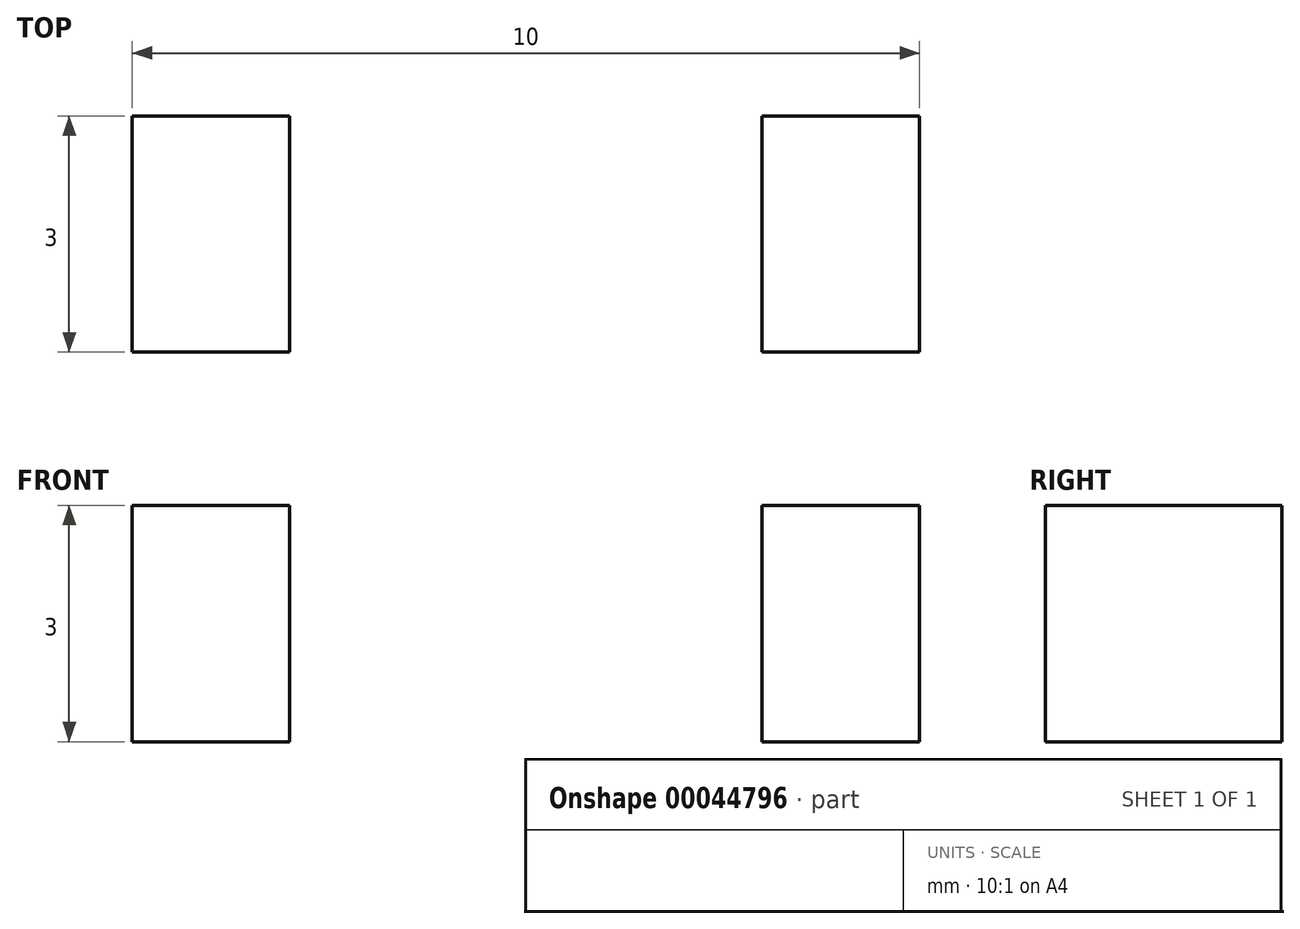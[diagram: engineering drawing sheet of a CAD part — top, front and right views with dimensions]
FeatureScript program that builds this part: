
annotation { "Feature Type Name" : "Feature", "Feature Type Description" : "" }
export const myFeature = defineFeature(function(context is Context, id is Id, definition is map)
    precondition{}
    {
        {
            var Q0;
            Q0=qCreatedBy(makeId("Front.planeOp"),FACE);
            var sketch = newSketch(context, id + "F0", { "sketchPlane" : qUnion([Q0])});
            skLineSegment(sketch, "E0.rect.bottom", {"start": v(5, 42) * mm, "end": v(-5, 42) * mm});
            skLineSegment(sketch, "E0.rect.top", {"start": v(5, -42) * mm, "end": v(-5, -42) * mm});
            skLineSegment(sketch, "E0.rect.left", {"start": v(5, 42) * mm, "end": v(5, -42) * mm});
            skLineSegment(sketch, "E0.rect.right", {"start": v(-5, 42) * mm, "end": v(-5, -42) * mm});
            skPoint(sketch, "E0.rect.middle", {"position": v(0, 0) * mm});
            skLineSegment(sketch, "E1", {"start": v(0, 42) * mm, "end": v(0, -42) * mm, "construction": true});
            skCircle(sketch, "E2", {"center": v(0, 27) * mm, "radius": 1.5 * mm});
            skCircle(sketch, "E3", {"center": v(0, -33) * mm, "radius": 1.5 * mm});
            skLineSegment(sketch, "E4.bottom", {"start": v(-5, 22) * mm, "end": v(-3, 22) * mm});
            skLineSegment(sketch, "E4.top", {"start": v(-5, 25) * mm, "end": v(-3, 25) * mm});
            skLineSegment(sketch, "E4.left", {"start": v(-5, 22) * mm, "end": v(-5, 25) * mm});
            skLineSegment(sketch, "E4.right", {"start": v(-3, 22) * mm, "end": v(-3, 25) * mm});
            skLineSegment(sketch, "E5.bottom", {"start": v(5, 22) * mm, "end": v(3, 22) * mm});
            skLineSegment(sketch, "E5.top", {"start": v(5, 25) * mm, "end": v(3, 25) * mm});
            skLineSegment(sketch, "E5.left", {"start": v(5, 22) * mm, "end": v(5, 25) * mm});
            skLineSegment(sketch, "E5.right", {"start": v(3, 22) * mm, "end": v(3, 25) * mm});
            skLineSegment(sketch, "E6.bottom", {"start": v(-5, -31) * mm, "end": v(-3, -31) * mm});
            skLineSegment(sketch, "E6.top", {"start": v(-5, -28) * mm, "end": v(-3, -28) * mm});
            skLineSegment(sketch, "E6.left", {"start": v(-5, -31) * mm, "end": v(-5, -28) * mm});
            skLineSegment(sketch, "E6.right", {"start": v(-3, -31) * mm, "end": v(-3, -28) * mm});
            skLineSegment(sketch, "E7.bottom", {"start": v(5, -31) * mm, "end": v(3, -31) * mm});
            skLineSegment(sketch, "E7.top", {"start": v(5, -28) * mm, "end": v(3, -28) * mm});
            skLineSegment(sketch, "E7.left", {"start": v(5, -31) * mm, "end": v(5, -28) * mm});
            skLineSegment(sketch, "E7.right", {"start": v(3, -31) * mm, "end": v(3, -28) * mm});
            skLineSegment(sketch, "E8.bottom", {"start": v(-5, 42) * mm, "end": v(-3, 42) * mm});
            skLineSegment(sketch, "E8.top", {"start": v(-5, 39) * mm, "end": v(-3, 39) * mm});
            skLineSegment(sketch, "E8.left", {"start": v(-5, 42) * mm, "end": v(-5, 39) * mm});
            skLineSegment(sketch, "E8.right", {"start": v(-3, 42) * mm, "end": v(-3, 39) * mm});
            skLineSegment(sketch, "E9.bottom", {"start": v(5, 42) * mm, "end": v(3, 42) * mm});
            skLineSegment(sketch, "E9.top", {"start": v(5, 39) * mm, "end": v(3, 39) * mm});
            skLineSegment(sketch, "E9.left", {"start": v(5, 42) * mm, "end": v(5, 39) * mm});
            skLineSegment(sketch, "E9.right", {"start": v(3, 42) * mm, "end": v(3, 39) * mm});
            skLineSegment(sketch, "E10.bottom", {"start": v(-5, -42) * mm, "end": v(-3, -42) * mm});
            skLineSegment(sketch, "E10.top", {"start": v(-5, -39) * mm, "end": v(-3, -39) * mm});
            skLineSegment(sketch, "E10.left", {"start": v(-5, -42) * mm, "end": v(-5, -39) * mm});
            skLineSegment(sketch, "E10.right", {"start": v(-3, -42) * mm, "end": v(-3, -39) * mm});
            skLineSegment(sketch, "E11.bottom", {"start": v(5, -42) * mm, "end": v(3, -42) * mm});
            skLineSegment(sketch, "E11.top", {"start": v(5, -39) * mm, "end": v(3, -39) * mm});
            skLineSegment(sketch, "E11.left", {"start": v(5, -42) * mm, "end": v(5, -39) * mm});
            skLineSegment(sketch, "E11.right", {"start": v(3, -42) * mm, "end": v(3, -39) * mm});
            skSolve(sketch);
        }
        {
            var Q0;
            Q0=makeQuery(id+"F0.imprint","IMPRINT",FACE,{"disambiguationData":[TD([[makeQuery(id+"F0.imprint","IMPRINT",EDGE,{"derivedFrom":sQuery(id+"F0.wireOp",EDGE,"E0.rect.bottom")}),1.0]])]});
            extrude(context, id + "F1", {"entities" : qUnion([Q0]), "depth" : 3 * mm});
        }
    });
